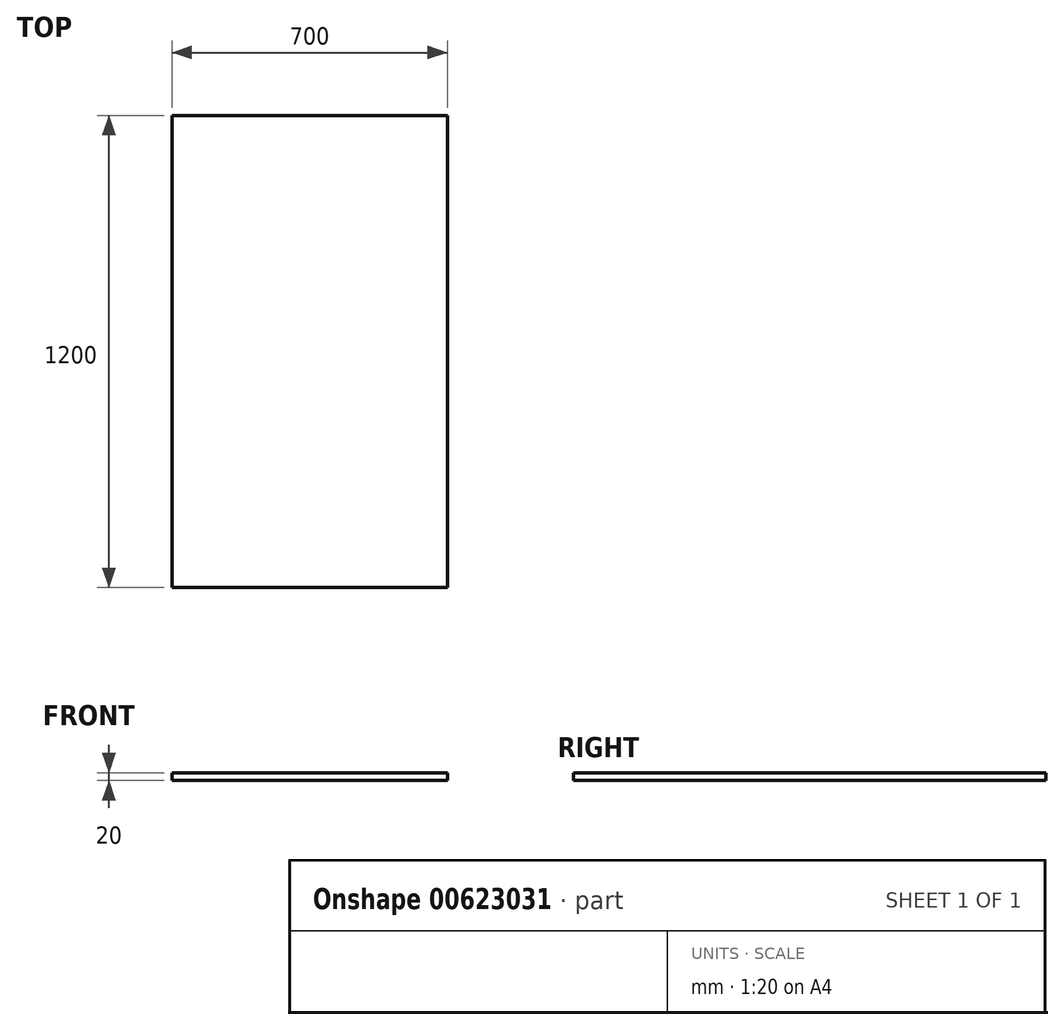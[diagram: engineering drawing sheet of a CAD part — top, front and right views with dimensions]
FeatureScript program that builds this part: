
annotation { "Feature Type Name" : "Feature", "Feature Type Description" : "" }
export const myFeature = defineFeature(function(context is Context, id is Id, definition is map)
    precondition{}
    {
        {
            var Q0;
            Q0=qCreatedBy(makeId("Top.planeOp"),FACE);
            var sketch = newSketch(context, id + "F0", { "sketchPlane" : qUnion([Q0])});
            skLineSegment(sketch, "E0.bottom", {"start": v(0, 0) * mm, "end": v(700, 0) * mm});
            skLineSegment(sketch, "E0.top", {"start": v(0, 1200) * mm, "end": v(700, 1200) * mm});
            skLineSegment(sketch, "E0.left", {"start": v(0, 0) * mm, "end": v(0, 1200) * mm});
            skLineSegment(sketch, "E0.right", {"start": v(700, 0) * mm, "end": v(700, 1200) * mm});
            skSolve(sketch);
        }
        {
            var Q0;
            Q0 = qSketchRegion(id + "F0", true);
            extrude(context, id + "F1", {"entities" : qUnion([Q0]), "depth" : 20 * mm, "offsetDistance" : 25 * mm});
        }
    });
